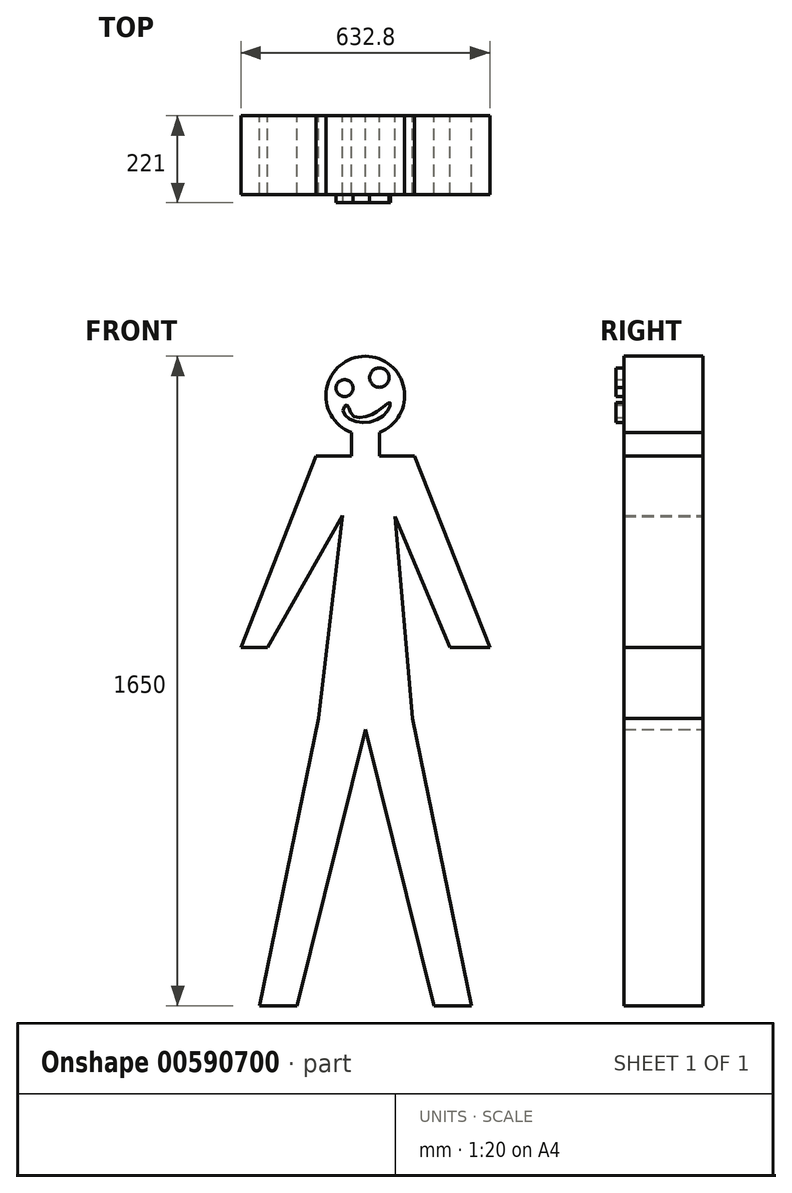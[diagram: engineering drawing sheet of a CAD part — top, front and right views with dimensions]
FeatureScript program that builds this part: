
annotation { "Feature Type Name" : "Feature", "Feature Type Description" : "" }
export const myFeature = defineFeature(function(context is Context, id is Id, definition is map)
    precondition{}
    {
        {
            var Q0;
            Q0=qCreatedBy(makeId("Front.planeOp"),FACE);
            var sketch = newSketch(context, id + "F0", { "sketchPlane" : qUnion([Q0])});
            skArc(sketch, "E0", {"start": v(0, 1210.86) * mm, "mid": v(-98.35, 1128.97) * mm, "end": v(-35.61, 1017.42) * mm});
            skLineSegment(sketch, "E1", {"start": v(0, 262.87) * mm, "end": v(-173.84, -439.14) * mm});
            skLineSegment(sketch, "E2", {"start": v(-173.84, -439.14) * mm, "end": v(-269.39, -439.14) * mm});
            skLineSegment(sketch, "E3", {"start": v(-269.39, -439.14) * mm, "end": v(-119.45, 290.82) * mm});
            skLineSegment(sketch, "E4", {"start": v(-119.45, 290.82) * mm, "end": v(-57.55, 806.79) * mm});
            skLineSegment(sketch, "E5", {"start": v(-57.55, 806.79) * mm, "end": v(-248.2, 470.77) * mm});
            skLineSegment(sketch, "E6", {"start": v(-248.2, 470.77) * mm, "end": v(-316.4, 470.77) * mm});
            skLineSegment(sketch, "E7", {"start": v(-316.4, 470.77) * mm, "end": v(-124.77, 957.83) * mm});
            skLineSegment(sketch, "E8", {"start": v(-124.77, 957.83) * mm, "end": v(-35.61, 957.83) * mm});
            skLineSegment(sketch, "E9", {"start": v(-35.61, 1017.42) * mm, "end": v(-35.61, 957.83) * mm});
            skLineSegment(sketch, "E10.MirrorCS", {"start": v(124.77, 957.83) * mm, "end": v(35.61, 957.83) * mm});
            skLineSegment(sketch, "E11.MirrorCS", {"start": v(35.61, 1017.42) * mm, "end": v(35.61, 957.83) * mm});
            skLineSegment(sketch, "E12.MirrorCS", {"start": v(214.47, 470.77) * mm, "end": v(316.4, 470.77) * mm});
            skLineSegment(sketch, "E13.MirrorCS", {"start": v(173.84, -439.14) * mm, "end": v(269.39, -439.14) * mm});
            skArc(sketch, "E14.MirrorCS", {"start": v(0, 1210.86) * mm, "mid": v(98.35, 1128.97) * mm, "end": v(35.61, 1017.42) * mm});
            skLineSegment(sketch, "E15.MirrorCS", {"start": v(0, 262.87) * mm, "end": v(173.84, -439.14) * mm});
            skLineSegment(sketch, "E16.MirrorCS", {"start": v(316.4, 470.77) * mm, "end": v(124.77, 957.83) * mm});
            skLineSegment(sketch, "E17.MirrorCS", {"start": v(269.39, -439.14) * mm, "end": v(119.45, 290.82) * mm});
            skLineSegment(sketch, "E18.MirrorCS", {"start": v(75.13, 803.97) * mm, "end": v(214.47, 470.77) * mm});
            skLineSegment(sketch, "E19.MirrorCS", {"start": v(119.45, 290.82) * mm, "end": v(75.13, 803.97) * mm});
            skSolve(sketch);
        }
        {
            var Q0;
            Q0=makeQuery(id+"F0.imprint","IMPRINT",FACE,{"disambiguationData":[TD([[makeQuery(id+"F0.imprint","IMPRINT",EDGE,{"derivedFrom":sQuery(id+"F0.wireOp",EDGE,"E0")}),1.0]])]});
            extrude(context, id + "F1", {"entities" : qUnion([Q0]), "endBound" : BoundingType.SYMMETRIC, "depth" : 200 * mm, "offsetDistance" : 25 * mm});
        }
        {
            var Q0;
            Q0=makeQuery(id+"F1.opExtrude","CAP_FACE",FACE,{"disambiguationData":[OSD([sQuery(id+"F0.wireOp",EDGE,"E0"),sQuery(id+"F0.wireOp",EDGE,"E1"),sQuery(id+"F0.wireOp",EDGE,"E2"),sQuery(id+"F0.wireOp",EDGE,"E3"),sQuery(id+"F0.wireOp",EDGE,"E4"),sQuery(id+"F0.wireOp",EDGE,"E5"),sQuery(id+"F0.wireOp",EDGE,"E6"),sQuery(id+"F0.wireOp",EDGE,"E7"),sQuery(id+"F0.wireOp",EDGE,"E8"),sQuery(id+"F0.wireOp",EDGE,"E9"),sQuery(id+"F0.wireOp",EDGE,"E10.MirrorCS"),sQuery(id+"F0.wireOp",EDGE,"E11.MirrorCS"),sQuery(id+"F0.wireOp",EDGE,"E12.MirrorCS"),sQuery(id+"F0.wireOp",EDGE,"E13.MirrorCS"),sQuery(id+"F0.wireOp",EDGE,"E14.MirrorCS"),sQuery(id+"F0.wireOp",EDGE,"E15.MirrorCS"),sQuery(id+"F0.wireOp",EDGE,"E16.MirrorCS"),sQuery(id+"F0.wireOp",EDGE,"E17.MirrorCS"),sQuery(id+"F0.wireOp",EDGE,"E18.MirrorCS"),sQuery(id+"F0.wireOp",EDGE,"E19.MirrorCS")])],"isStart":false});
            var sketch = newSketch(context, id + "F2", { "sketchPlane" : qUnion([Q0])});
            skCircle(sketch, "E20", {"center": v(-52.7, 1129.87) * mm, "radius": 21.59 * mm});
            skCircle(sketch, "E21", {"center": v(35.61, 1156.69) * mm, "radius": 24.62 * mm});
            skFitSpline(sketch, "E22", {"points": [v(-56.2, 1072.73) * mm, v(-18.34, 1043.4) * mm, v(49.91, 1063.95) * mm, v(62.76, 1093) * mm, v(50.04, 1085.79) * mm, v(16.64, 1063.23) * mm, v(-32.5, 1060.77) * mm, v(-46.6, 1086.88) * mm, v(-56.2, 1072.73) * mm]});
            skSolve(sketch);
        }
        {
            var Q0;
            Q0 = qSketchRegion(id + "F2", true);
            extrude(context, id + "F3", {"entities" : qUnion([Q0]), "operationType" : NewBodyOperationType.ADD, "depth" : 21 * mm, "offsetDistance" : 25 * mm});
        }
    });
